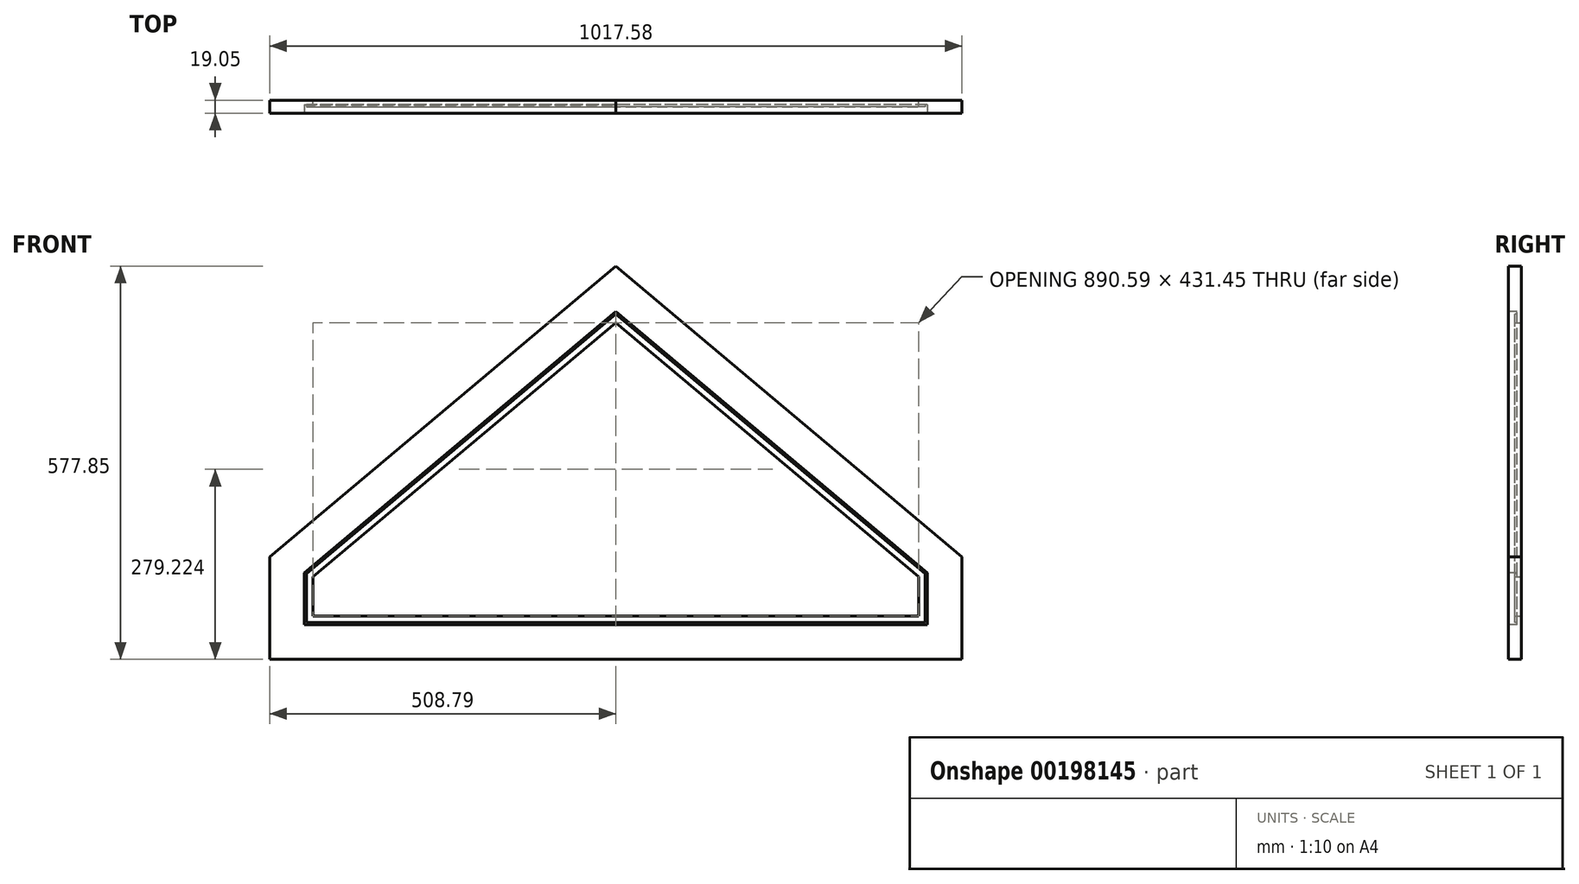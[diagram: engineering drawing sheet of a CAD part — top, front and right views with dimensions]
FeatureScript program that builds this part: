
annotation { "Feature Type Name" : "Feature", "Feature Type Description" : "" }
export const myFeature = defineFeature(function(context is Context, id is Id, definition is map)
    precondition{}
    {
        {
            var Q0;
            Q0=qCreatedBy(makeId("Front.planeOp"),FACE);
            var sketch = newSketch(context, id + "F0", { "sketchPlane" : qUnion([Q0])});
            skLineSegment(sketch, "E0", {"start": v(0, 0) * mm, "end": v(-508.8, 0) * mm});
            skLineSegment(sketch, "E1", {"start": v(-508.8, 0) * mm, "end": v(-508.8, 150.81) * mm});
            skLineSegment(sketch, "E2", {"start": v(-508.8, 150.81) * mm, "end": v(0, 577.85) * mm});
            skLineSegment(sketch, "E3", {"start": v(0, 577.85) * mm, "end": v(0, 0) * mm, "construction": true});
            skLineSegment(sketch, "E4.MirrorCS", {"start": v(508.8, 150.81) * mm, "end": v(0, 577.85) * mm});
            skLineSegment(sketch, "E5.MirrorCS", {"start": v(0, 0) * mm, "end": v(508.8, 0) * mm});
            skLineSegment(sketch, "E6.MirrorCS", {"start": v(508.8, 0) * mm, "end": v(508.8, 150.81) * mm});
            skLineSegment(sketch, "E7.0", {"start": v(-445.3, 63.5) * mm, "end": v(-445.3, 121.2) * mm});
            skLineSegment(sketch, "E7.1", {"start": v(445.3, 121.2) * mm, "end": v(0, 494.95) * mm});
            skLineSegment(sketch, "E7.2", {"start": v(445.3, 63.5) * mm, "end": v(445.3, 121.2) * mm});
            skLineSegment(sketch, "E7.3", {"start": v(-445.3, 121.2) * mm, "end": v(0, 494.95) * mm});
            skLineSegment(sketch, "E7.4", {"start": v(0, 63.5) * mm, "end": v(445.3, 63.5) * mm});
            skLineSegment(sketch, "E7.5", {"start": v(0, 63.5) * mm, "end": v(-445.3, 63.5) * mm});
            skLineSegment(sketch, "E8", {"start": v(-508.8, 150.81) * mm, "end": v(-445.3, 121.2) * mm, "construction": true});
            skLineSegment(sketch, "E9", {"start": v(508.8, 150.81) * mm, "end": v(445.3, 121.2) * mm, "construction": true});
            skSolve(sketch);
        }
        {
            var Q0;
            Q0=makeQuery(id+"F0.imprint","IMPRINT",FACE,{"disambiguationData":[TD([[makeQuery(id+"F0.imprint","IMPRINT",EDGE,{"derivedFrom":sQuery(id+"F0.wireOp",EDGE,"E0")}),-1.0]])]});
            extrude(context, id + "F1", {"entities" : qUnion([Q0]), "depth" : 19.05 * mm});
        }
        {
            var Q0;
            Q0=makeQuery(id+"F1.opExtrude","CAP_FACE",FACE,{"disambiguationData":[OSD([sQuery(id+"F0.wireOp",EDGE,"E0"),sQuery(id+"F0.wireOp",EDGE,"E1"),sQuery(id+"F0.wireOp",EDGE,"E2"),sQuery(id+"F0.wireOp",EDGE,"E4.MirrorCS"),sQuery(id+"F0.wireOp",EDGE,"E5.MirrorCS"),sQuery(id+"F0.wireOp",EDGE,"E6.MirrorCS"),sQuery(id+"F0.wireOp",EDGE,"E7.0"),sQuery(id+"F0.wireOp",EDGE,"E7.1"),sQuery(id+"F0.wireOp",EDGE,"E7.2"),sQuery(id+"F0.wireOp",EDGE,"E7.3"),sQuery(id+"F0.wireOp",EDGE,"E7.4"),sQuery(id+"F0.wireOp",EDGE,"E7.5")])],"isStart":false});
            var sketch = newSketch(context, id + "F2", { "sketchPlane" : qUnion([Q0])});
            skSolve(sketch);
        }
        {
            var Q0;
            Q0=makeQuery(id+"F2.imprint","IMPRINT",FACE,{"disambiguationData":[TD([[makeQuery(id+"F2.imprint","IMPRINT",EDGE,{"derivedFrom":makeQuery(id+"F1.opExtrude","CAP_EDGE",EDGE,{"disambiguationData":[OSD([sQuery(id+"F0.wireOp",EDGE,"E1")])],"isStart":false})}),-1.0]])]});
            var sketch = newSketch(context, id + "F3", { "sketchPlane" : qUnion([Q0])});
            skLineSegment(sketch, "E10.0", {"start": v(458, 127.13) * mm, "end": v(0, 511.53) * mm});
            skLineSegment(sketch, "E10.1", {"start": v(-458, 127.13) * mm, "end": v(0, 511.53) * mm});
            skLineSegment(sketch, "E10.2", {"start": v(458, 50.8) * mm, "end": v(458, 127.13) * mm});
            skLineSegment(sketch, "E10.3", {"start": v(458, 50.8) * mm, "end": v(-458, 50.8) * mm});
            skLineSegment(sketch, "E10.4", {"start": v(-458, 50.8) * mm, "end": v(-458, 127.13) * mm});
            skLineSegment(sketch, "E11.0", {"start": v(-445.3, 121.2) * mm, "end": v(0, 494.95) * mm});
            skLineSegment(sketch, "E11.1", {"start": v(445.3, 121.2) * mm, "end": v(0, 494.95) * mm});
            skLineSegment(sketch, "E11.2", {"start": v(445.3, 63.5) * mm, "end": v(445.3, 121.2) * mm});
            skLineSegment(sketch, "E11.3", {"start": v(445.3, 63.5) * mm, "end": v(-445.3, 63.5) * mm});
            skLineSegment(sketch, "E11.4", {"start": v(-445.3, 63.5) * mm, "end": v(-445.3, 121.2) * mm});
            skSolve(sketch);
        }
        {
            var Q0;
            Q0 = qSketchRegion(id + "F3", true);
            extrude(context, id + "F4", {"entities" : qUnion([Q0]), "operationType" : NewBodyOperationType.REMOVE, "oppositeDirection" : true, "depth" : 9.52 * mm});
        }
        {
            var Q0;
            Q0=makeQuery(id+"F4.boolean.opBoolean","COPY",FACE,{"derivedFrom":makeQuery(id+"F4.opExtrude","CAP_FACE",FACE,{"disambiguationData":[OSD([sQuery(id+"F3.wireOp",EDGE,"E10.0"),sQuery(id+"F3.wireOp",EDGE,"E10.1"),sQuery(id+"F3.wireOp",EDGE,"E10.2"),sQuery(id+"F3.wireOp",EDGE,"E10.3"),sQuery(id+"F3.wireOp",EDGE,"E10.4"),sQuery(id+"F3.wireOp",EDGE,"E11.0"),sQuery(id+"F3.wireOp",EDGE,"E11.1"),sQuery(id+"F3.wireOp",EDGE,"E11.2"),sQuery(id+"F3.wireOp",EDGE,"E11.3"),sQuery(id+"F3.wireOp",EDGE,"E11.4")])],"isStart":false})});
            var sketch = newSketch(context, id + "F5", { "sketchPlane" : qUnion([Q0])});
            skLineSegment(sketch, "E12.0", {"start": v(-458, 127.13) * mm, "end": v(0, 511.53) * mm});
            skLineSegment(sketch, "E12.1", {"start": v(-458, 50.8) * mm, "end": v(-458, 127.13) * mm});
            skLineSegment(sketch, "E12.2", {"start": v(458, 50.8) * mm, "end": v(-458, 50.8) * mm});
            skLineSegment(sketch, "E12.3", {"start": v(458, 50.8) * mm, "end": v(458, 127.13) * mm});
            skLineSegment(sketch, "E12.4", {"start": v(458, 127.13) * mm, "end": v(0, 511.53) * mm});
            skLineSegment(sketch, "E13.0", {"start": v(454.82, 125.65) * mm, "end": v(0, 507.38) * mm});
            skLineSegment(sketch, "E13.1", {"start": v(454.82, 53.98) * mm, "end": v(454.82, 125.65) * mm});
            skLineSegment(sketch, "E13.2", {"start": v(-454.82, 125.65) * mm, "end": v(0, 507.38) * mm});
            skLineSegment(sketch, "E13.3", {"start": v(-454.82, 53.97) * mm, "end": v(-454.82, 125.65) * mm});
            skLineSegment(sketch, "E13.4", {"start": v(454.82, 53.98) * mm, "end": v(-454.82, 53.97) * mm});
            skSolve(sketch);
        }
        {
            var Q0;
            Q0 = qSketchRegion(id + "F5", true);
            extrude(context, id + "F6", {"entities" : qUnion([Q0]), "operationType" : NewBodyOperationType.REMOVE, "oppositeDirection" : true, "depth" : 3.17 * mm});
        }
    });
